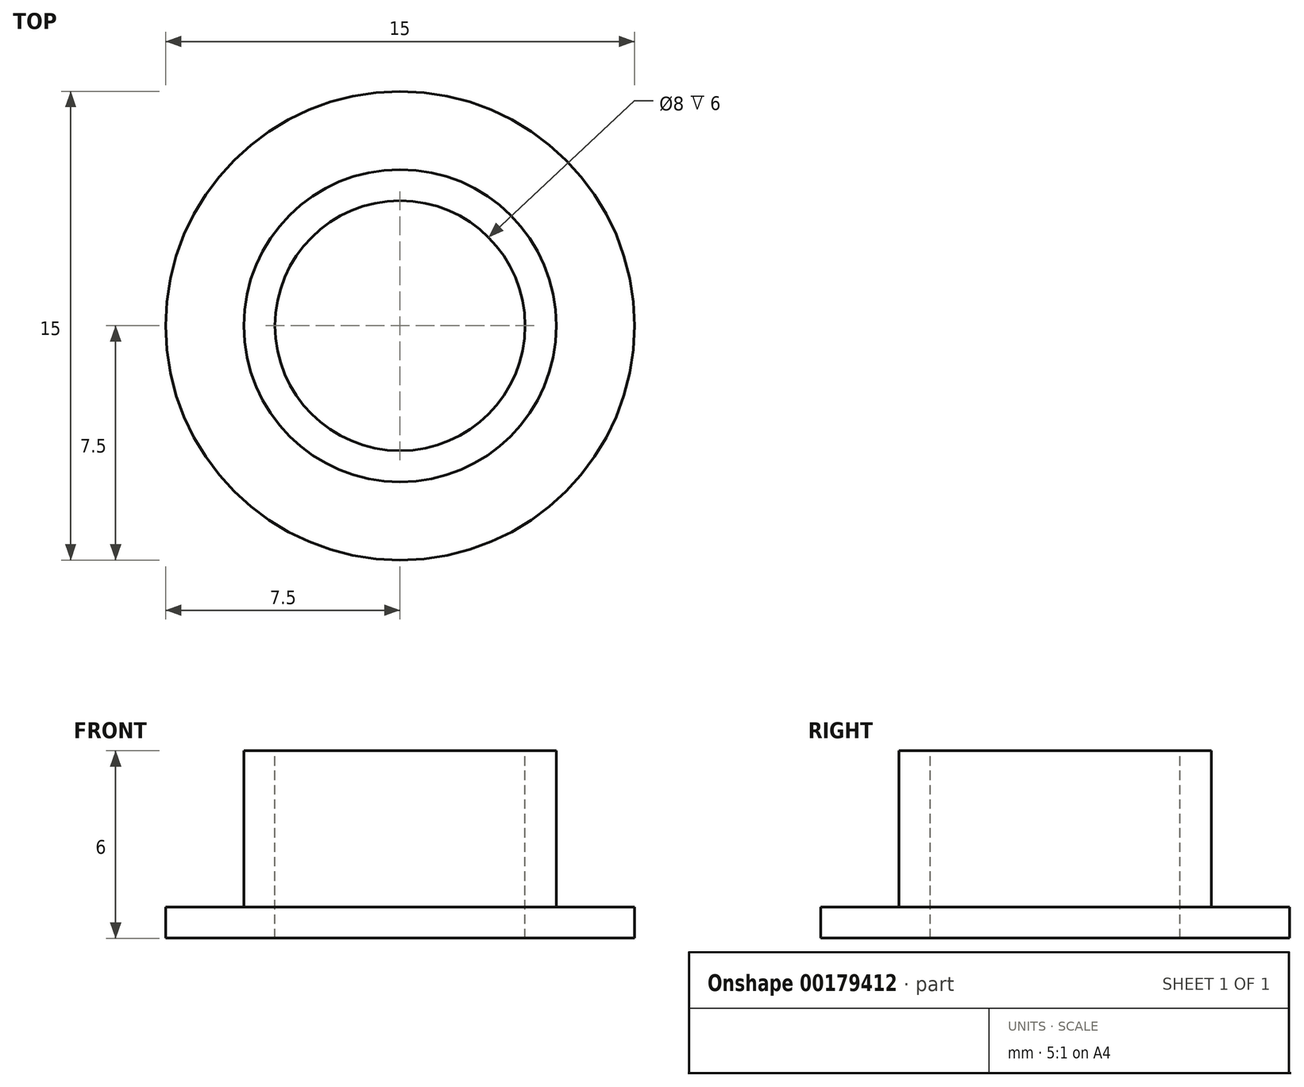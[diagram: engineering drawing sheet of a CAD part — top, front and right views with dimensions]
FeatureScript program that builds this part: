
annotation { "Feature Type Name" : "Feature", "Feature Type Description" : "" }
export const myFeature = defineFeature(function(context is Context, id is Id, definition is map)
    precondition{}
    {
        {
            var Q0;
            Q0=qCreatedBy(makeId("Front.planeOp"),FACE);
            var sketch = newSketch(context, id + "F0", { "sketchPlane" : qUnion([Q0])});
            skLineSegment(sketch, "E0.bottom", {"start": v(-5, -1.56) * mm, "end": v(-7.5, -1.56) * mm});
            skLineSegment(sketch, "E0.top", {"start": v(-4, -2.56) * mm, "end": v(-7.5, -2.56) * mm});
            skLineSegment(sketch, "E0.right", {"start": v(-7.5, -1.56) * mm, "end": v(-7.5, -2.56) * mm});
            skLineSegment(sketch, "E1.top", {"start": v(-4, 3.44) * mm, "end": v(-5, 3.44) * mm});
            skLineSegment(sketch, "E1.right", {"start": v(-5, -1.56) * mm, "end": v(-5, 3.44) * mm});
            skLineSegment(sketch, "E2", {"start": v(-4, 3.44) * mm, "end": v(-4, -2.56) * mm});
            skLineSegment(sketch, "E3", {"start": v(0, 6.81) * mm, "end": v(0, -6.9) * mm, "construction": true});
            skSolve(sketch);
        }
        {
            var Q0;
            Q0 = qSketchRegion(id + "F0", true);
            var Q1;
            Q1=sQuery(id+"F0.wireOp",EDGE,"E3");
            revolve(context, id + "F1", {"entities" : qUnion([Q0]), "axis" : qUnion([Q1]), "revolveType" : RevolveType.FULL});
        }
    });
